# Revit family: 0049390_Zephyr_SML_30W_4K_3300LM_1M_Class I
name_source: partatom
category: Lighting Fixtures
revit_build: Autodesk Revit 2017 (Build: 20160225_1515(x64)
units: mm (PartAtom-declared; Revit-internal decimal feet)

## family parameters
Always vertical = No
Cut with Voids When Loaded = No
Light Source = No
Part Type = Normal
Room Calculation Point = No
Round Connector Dimension = Use Diameter
Shared = No
Work Plane-Based = Yes

## types (1)
- 0049390-Zephyr Sml 3300LM 4K 1M GR Clas I
    Apparent Load = 30 VA
    Assembly Code = D5020200
    Beam Angle = 67.00°
    Body Material = Diecast Aluminium Grey-RAL9022
    CRI ( Ra ) = 70
    Catalog Number = 0049390
    Default Elevation = 0 mm  [stored 0 ft]
    Diffuser Material = UV Stabilised Polycarbonate
    Dimming Range = Non-dim / not dimmable (switched only)
    Distribution type = Medium Assymetric
    Drive Current = 750mA
    Electrical Protection = CLASS I
    Height = 78 mm  [stored 0.255906 ft]
    IK Rating = IK09
    IP Rating = IP66
    Initial Color = 4000 K
    Initial Intensity = 3300 lm
    LOR = 100%
    Lamp = Integrated LED
    Length = 359 mm  [stored 1.17782 ft]
    Life = 50 000h
    Light Loss Factor = 1
    Manufacturer = Feilo Sylvania
    Model = Zephyr Smal 3300LM Lantern 4000K 1M CLI Grey
    Product Family = Zephyr
    Ta Rating = 25
    Track adaptor type = 3-Circuit (L3)
    Voltage = 240 V
    Voltage Comments = UNV (Universal Voltage; 220-240 Volt)
    Weight = 1.50 kg
    Width = 161 mm  [stored 0.528215 ft]

note: [stored X ft] marks values corroborated as IEEE doubles in the binary element streams (Revit-internal decimal feet)

## geometry (parser evidence)
native form markers: Blend x2, Sweep x11
no freeform markers — native parametric forms only
